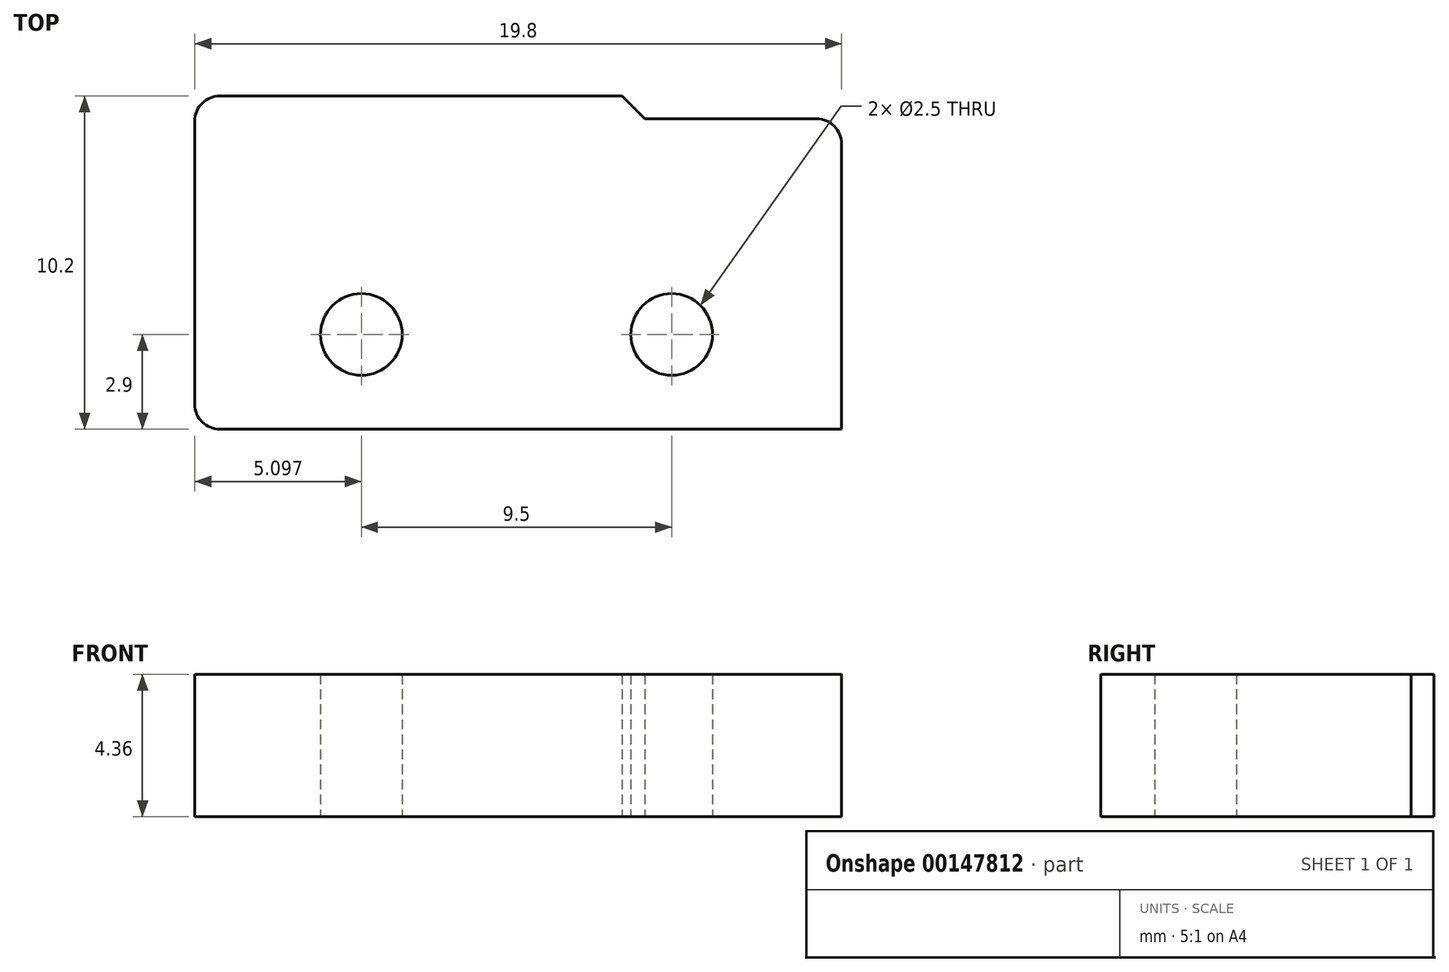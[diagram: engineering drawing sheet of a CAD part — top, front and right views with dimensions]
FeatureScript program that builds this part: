
annotation { "Feature Type Name" : "Feature", "Feature Type Description" : "" }
export const myFeature = defineFeature(function(context is Context, id is Id, definition is map)
    precondition{}
    {
        {
            var Q0;
            Q0=qCreatedBy(makeId("Top.planeOp"),FACE);
            var sketch = newSketch(context, id + "F0", { "sketchPlane" : qUnion([Q0])});
            skLineSegment(sketch, "E0", {"start": v(0, 0) * mm, "end": v(6.02, 0) * mm});
            skLineSegment(sketch, "E1", {"start": v(6.02, 0) * mm, "end": v(6.02, -9.5) * mm});
            skLineSegment(sketch, "E2", {"start": v(0, 0) * mm, "end": v(-0.7, 0.7) * mm});
            skLineSegment(sketch, "E3", {"start": v(6.02, 0) * mm, "end": v(6.02, 0.7) * mm, "construction": true});
            skLineSegment(sketch, "E4", {"start": v(-0.7, 0.7) * mm, "end": v(6.02, 0.7) * mm, "construction": true});
            skLineSegment(sketch, "E5.bottom", {"start": v(4.42, -9.5) * mm, "end": v(3.92, -9.5) * mm});
            skLineSegment(sketch, "E5.top", {"start": v(4.42, -13) * mm, "end": v(3.92, -13) * mm});
            skLineSegment(sketch, "E5.left", {"start": v(3.92, -9.5) * mm, "end": v(3.92, -13) * mm});
            skLineSegment(sketch, "E5.right", {"start": v(4.42, -9.5) * mm, "end": v(4.42, -13) * mm});
            skLineSegment(sketch, "E6.bottom", {"start": v(-3.13, -9.5) * mm, "end": v(-3.63, -9.5) * mm});
            skLineSegment(sketch, "E6.top", {"start": v(-3.13, -13) * mm, "end": v(-3.63, -13) * mm});
            skLineSegment(sketch, "E6.left", {"start": v(-3.13, -9.5) * mm, "end": v(-3.13, -13) * mm});
            skLineSegment(sketch, "E6.right", {"start": v(-3.63, -9.5) * mm, "end": v(-3.63, -13) * mm});
            skLineSegment(sketch, "E7.top", {"start": v(-11.68, -13) * mm, "end": v(-12.18, -13) * mm});
            skLineSegment(sketch, "E7.left", {"start": v(-12.18, -9.5) * mm, "end": v(-12.18, -13) * mm});
            skLineSegment(sketch, "E7.right", {"start": v(-11.68, -9.5) * mm, "end": v(-11.68, -13) * mm});
            skLineSegment(sketch, "E8", {"start": v(-0.7, 0.7) * mm, "end": v(-5.91, 0.7) * mm});
            skLineSegment(sketch, "E9", {"start": v(-5.91, 0.7) * mm, "end": v(-7.27, 0.7) * mm, "construction": true});
            skArc(sketch, "E10", {"start": v(-5.91, 0.7) * mm, "mid": v(-6.6, 1.38) * mm, "end": v(-7.27, 0.7) * mm});
            skLineSegment(sketch, "E11", {"start": v(-7.27, 0.7) * mm, "end": v(-9.81, 0.7) * mm});
            skLineSegment(sketch, "E12", {"start": v(-9.81, 0.7) * mm, "end": v(-9.81, 1.1) * mm});
            skArc(sketch, "E13", {"start": v(-9.51, 1.4) * mm, "mid": v(-9.73, 1.32) * mm, "end": v(-9.81, 1.1) * mm});
            skLineSegment(sketch, "E14", {"start": v(-9.51, 1.4) * mm, "end": v(6.02, 1.4) * mm});
            skLineSegment(sketch, "E15", {"start": v(6.02, 1.4) * mm, "end": v(6.02, 2.2) * mm});
            skLineSegment(sketch, "E16", {"start": v(1.22, 2.2) * mm, "end": v(-9.51, 2.2) * mm});
            skArc(sketch, "E17", {"start": v(-9.51, 2.2) * mm, "mid": v(-10.29, 1.88) * mm, "end": v(-10.6, 1.1) * mm});
            skLineSegment(sketch, "E18", {"start": v(-10.6, 1.1) * mm, "end": v(-10.6, 0.7) * mm});
            skLineSegment(sketch, "E19", {"start": v(-10.6, 0.7) * mm, "end": v(-9.81, 0.7) * mm});
            skLineSegment(sketch, "E20", {"start": v(-8.68, -9.5) * mm, "end": v(-8.68, -6.6) * mm, "construction": true});
            skLineSegment(sketch, "E21", {"start": v(-8.68, -6.6) * mm, "end": v(-13.78, -6.6) * mm, "construction": true});
            skLineSegment(sketch, "E22", {"start": v(-13.78, -9.5) * mm, "end": v(-13.78, 0.7) * mm});
            skCircle(sketch, "E23", {"center": v(-8.68, -6.6) * mm, "radius": 1.25 * mm});
            skLineSegment(sketch, "E24", {"start": v(-8.68, -6.6) * mm, "end": v(0.82, -6.6) * mm, "construction": true});
            skCircle(sketch, "E25", {"center": v(0.82, -6.6) * mm, "radius": 1.25 * mm});
            skLineSegment(sketch, "E26", {"start": v(-13.78, -9.5) * mm, "end": v(-12.18, -9.5) * mm});
            skLineSegment(sketch, "E27", {"start": v(-12.18, -9.5) * mm, "end": v(-11.68, -9.5) * mm});
            skLineSegment(sketch, "E28", {"start": v(-11.68, -9.5) * mm, "end": v(-3.63, -9.5) * mm});
            skPoint(sketch, "E29", {"position": v(-3.38, -13) * mm});
            skLineSegment(sketch, "E30", {"start": v(6.02, -9.5) * mm, "end": v(4.42, -9.5) * mm});
            skLineSegment(sketch, "E31", {"start": v(3.92, -9.5) * mm, "end": v(-3.13, -9.5) * mm});
            skLineSegment(sketch, "E32", {"start": v(-13.78, 0.7) * mm, "end": v(-10.6, 0.7) * mm});
            skLineSegment(sketch, "E33.bottom", {"start": v(6.02, 2.2) * mm, "end": v(1.22, 2.2) * mm, "construction": true});
            skLineSegment(sketch, "E33.top", {"start": v(6.02, 4.6) * mm, "end": v(1.22, 4.6) * mm, "construction": true});
            skLineSegment(sketch, "E33.left", {"start": v(6.02, 2.2) * mm, "end": v(6.02, 4.6) * mm});
            skLineSegment(sketch, "E33.right", {"start": v(1.22, 2.2) * mm, "end": v(1.22, 4.6) * mm});
            skArc(sketch, "E34", {"start": v(6.02, 4.6) * mm, "mid": v(3.62, 7) * mm, "end": v(1.22, 4.6) * mm});
            skArc(sketch, "E35", {"start": v(1.22, 4.6) * mm, "mid": v(3.62, 2.2) * mm, "end": v(6.02, 4.6) * mm, "construction": true});
            skSolve(sketch);
        }
        {
            var Q0;
            Q0=makeQuery(id+"F0.imprint","IMPRINT",FACE,{"disambiguationData":[TD([[makeQuery(id+"F0.imprint","IMPRINT",EDGE,{"derivedFrom":sQuery(id+"F0.wireOp",EDGE,"E5.bottom")}),1.0]])]});
            var Q1;
            Q1=makeQuery(id+"F0.imprint","IMPRINT",FACE,{"disambiguationData":[TD([[makeQuery(id+"F0.imprint","IMPRINT",EDGE,{"derivedFrom":sQuery(id+"F0.wireOp",EDGE,"E6.bottom")}),1.0]])]});
            var Q2;
            Q2=makeQuery(id+"F0.imprint","IMPRINT",FACE,{"disambiguationData":[TD([[makeQuery(id+"F0.imprint","IMPRINT",EDGE,{"derivedFrom":sQuery(id+"F0.wireOp",EDGE,"E7.top")}),-1.0]])]});
            var Q3;
            Q3=makeQuery(id+"F0.imprint","IMPRINT",FACE,{"disambiguationData":[TD([[makeQuery(id+"F0.imprint","IMPRINT",EDGE,{"derivedFrom":sQuery(id+"F0.wireOp",EDGE,"E12")}),1.0]])]});
            var Q4;
            Q4=makeQuery(id+"F0.imprint","IMPRINT",FACE,{"disambiguationData":[TD([[makeQuery(id+"F0.imprint","IMPRINT",EDGE,{"derivedFrom":sQuery(id+"F0.wireOp",EDGE,"E0")}),-1.0]])]});
            var Q5;
            {var subQ1=sQuery(id+"F0.wireOp",EDGE,"E11");Q5=makeQuery(id+"F0.imprint","IMPRINT",FACE,{"disambiguationData":[TD([[makeQuery(id+"F0.imprint","IMPRINT",EDGE,{"derivedFrom":subQ1}),-1.0]])]});}
            extrude(context, id + "F1", {"entities" : qUnion([Q0, Q1, Q2, Q3, Q4, Q5]), "depth" : 4.36 * mm});
        }
        {
            var Q0;
            Q0=makeQuery(id+"FPg2b6c1lyLBN3m_1.boolean.opBoolean","INTERSECT",EDGE,{"derivedFrom":[makeQuery(id+"FPg2b6c1lyLBN3m_1.opExtrude","SWEPT_FACE",FACE,{"disambiguationData":[OSD([sQuery(id+"FlYVYaWIL6B6KNc_1.wireOp",EDGE,"nrUYbUd8-JSl6-swZw-RmJb-maEEpmxHUWtH.left")])]}),makeQuery(id+"FPg2b6c1lyLBN3m_1.opExtrude","SWEPT_FACE",FACE,{"disambiguationData":[OSD([sQuery(id+"FlYVYaWIL6B6KNc_1.wireOp",EDGE,"Yd5q5QGT-WIuf-AyGf-YbjL-hEvO9SgvATE9.left")])]})]});
            var Q1;
            Q1=makeQuery(id+"F1.opExtrude","SWEPT_EDGE",EDGE,{"disambiguationData":[OSD([sQuery(id+"F0.wireOp",EDGE,"E0"),sQuery(id+"F0.wireOp",EDGE,"E1")])]});
            var Q2;
            Q2=makeQuery(id+"F1.opExtrude","SWEPT_EDGE",EDGE,{"disambiguationData":[OSD([sQuery(id+"F0.wireOp",EDGE,"E22"),sQuery(id+"F0.wireOp",EDGE,"E26")])]});
            var Q3;
            Q3=makeQuery(id+"F1.opExtrude","SWEPT_EDGE",EDGE,{"disambiguationData":[OSD([sQuery(id+"F0.wireOp",EDGE,"E22"),sQuery(id+"F0.wireOp",EDGE,"E32")])]});
            fillet(context, id + "F2", {"entities" : qUnion([Q0, Q1, Q2, Q3]), "radius" : 0.76 * mm, "tangentPropagation" : true, "allowEdgeOverflow" : false});
        }
        {
            var Q0;
            Q0=makeQuery(id+"F1.opExtrude","CAP_FACE",FACE,{"disambiguationData":[OSD([sQuery(id+"F0.wireOp",EDGE,"E0"),sQuery(id+"F0.wireOp",EDGE,"E1"),sQuery(id+"F0.wireOp",EDGE,"E2"),sQuery(id+"F0.wireOp",EDGE,"E5.top"),sQuery(id+"F0.wireOp",EDGE,"E5.left"),sQuery(id+"F0.wireOp",EDGE,"E5.right"),sQuery(id+"F0.wireOp",EDGE,"E6.top"),sQuery(id+"F0.wireOp",EDGE,"E6.left"),sQuery(id+"F0.wireOp",EDGE,"E6.right"),sQuery(id+"F0.wireOp",EDGE,"E7.top"),sQuery(id+"F0.wireOp",EDGE,"E7.left"),sQuery(id+"F0.wireOp",EDGE,"E7.right"),sQuery(id+"F0.wireOp",EDGE,"E8"),sQuery(id+"F0.wireOp",EDGE,"E10"),sQuery(id+"F0.wireOp",EDGE,"E11"),sQuery(id+"F0.wireOp",EDGE,"E12"),sQuery(id+"F0.wireOp",EDGE,"E13"),sQuery(id+"F0.wireOp",EDGE,"E14"),sQuery(id+"F0.wireOp",EDGE,"E15"),sQuery(id+"F0.wireOp",EDGE,"E16"),sQuery(id+"F0.wireOp",EDGE,"E17"),sQuery(id+"F0.wireOp",EDGE,"E18"),sQuery(id+"F0.wireOp",EDGE,"E22"),sQuery(id+"F0.wireOp",EDGE,"E23"),sQuery(id+"F0.wireOp",EDGE,"E25"),sQuery(id+"F0.wireOp",EDGE,"E26"),sQuery(id+"F0.wireOp",EDGE,"E28"),sQuery(id+"F0.wireOp",EDGE,"E30"),sQuery(id+"F0.wireOp",EDGE,"E31"),sQuery(id+"F0.wireOp",EDGE,"E32"),sQuery(id+"F0.wireOp",EDGE,"E33.left"),sQuery(id+"F0.wireOp",EDGE,"E33.right"),sQuery(id+"F0.wireOp",EDGE,"E34")])],"isStart":false});
            var sketch = newSketch(context, id + "F3", { "sketchPlane" : qUnion([Q0])});
            skLineSegment(sketch, "E36.bottom", {"start": v(-13.02, 0.7) * mm, "end": v(6.02, 0.7) * mm});
            skLineSegment(sketch, "E36.top", {"start": v(-13.02, 7) * mm, "end": v(6.02, 7) * mm});
            skLineSegment(sketch, "E36.left", {"start": v(-13.02, 0.7) * mm, "end": v(-13.02, 7) * mm});
            skLineSegment(sketch, "E36.right", {"start": v(6.02, 0.7) * mm, "end": v(6.02, 7) * mm});
            skLineSegment(sketch, "E37.bottom", {"start": v(6.02, -9.5) * mm, "end": v(-13.02, -9.5) * mm});
            skLineSegment(sketch, "E37.top", {"start": v(6.02, -13) * mm, "end": v(-13.02, -13) * mm});
            skLineSegment(sketch, "E37.left", {"start": v(6.02, -9.5) * mm, "end": v(6.02, -13) * mm});
            skLineSegment(sketch, "E37.right", {"start": v(-13.02, -9.5) * mm, "end": v(-13.02, -13) * mm});
            skSolve(sketch);
        }
        {
            var Q0;
            Q0=qSketchRegion(id+"F3",true);
            var Q1;
            Q1=makeQuery(id+"F1.opExtrude","CAP_FACE",FACE,{"disambiguationData":[OSD([sQuery(id+"F0.wireOp",EDGE,"E0"),sQuery(id+"F0.wireOp",EDGE,"E1"),sQuery(id+"F0.wireOp",EDGE,"E2"),sQuery(id+"F0.wireOp",EDGE,"E5.top"),sQuery(id+"F0.wireOp",EDGE,"E5.left"),sQuery(id+"F0.wireOp",EDGE,"E5.right"),sQuery(id+"F0.wireOp",EDGE,"E6.top"),sQuery(id+"F0.wireOp",EDGE,"E6.left"),sQuery(id+"F0.wireOp",EDGE,"E6.right"),sQuery(id+"F0.wireOp",EDGE,"E7.top"),sQuery(id+"F0.wireOp",EDGE,"E7.left"),sQuery(id+"F0.wireOp",EDGE,"E7.right"),sQuery(id+"F0.wireOp",EDGE,"E8"),sQuery(id+"F0.wireOp",EDGE,"E10"),sQuery(id+"F0.wireOp",EDGE,"E11"),sQuery(id+"F0.wireOp",EDGE,"E12"),sQuery(id+"F0.wireOp",EDGE,"E13"),sQuery(id+"F0.wireOp",EDGE,"E14"),sQuery(id+"F0.wireOp",EDGE,"E15"),sQuery(id+"F0.wireOp",EDGE,"E16"),sQuery(id+"F0.wireOp",EDGE,"E17"),sQuery(id+"F0.wireOp",EDGE,"E18"),sQuery(id+"F0.wireOp",EDGE,"E22"),sQuery(id+"F0.wireOp",EDGE,"E23"),sQuery(id+"F0.wireOp",EDGE,"E25"),sQuery(id+"F0.wireOp",EDGE,"E26"),sQuery(id+"F0.wireOp",EDGE,"E28"),sQuery(id+"F0.wireOp",EDGE,"E30"),sQuery(id+"F0.wireOp",EDGE,"E31"),sQuery(id+"F0.wireOp",EDGE,"E32"),sQuery(id+"F0.wireOp",EDGE,"E33.left"),sQuery(id+"F0.wireOp",EDGE,"E33.right"),sQuery(id+"F0.wireOp",EDGE,"E34")])],"isStart":true});
            extrude(context, id + "F4", {"entities" : qUnion([Q0]), "operationType" : NewBodyOperationType.REMOVE, "endBound" : BoundingType.UP_TO_SURFACE, "oppositeDirection" : true, "endBoundEntityFace" : qUnion([Q1]), "depth" : 25.4 * mm});
        }
    });
